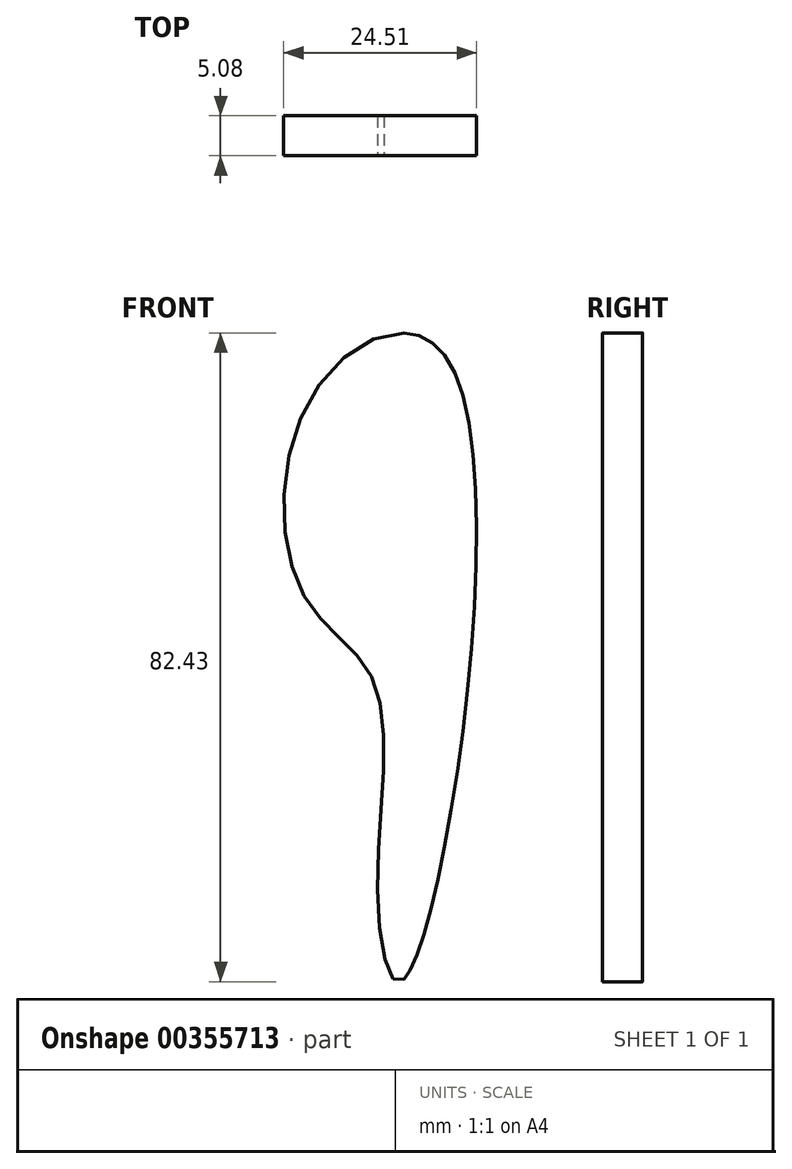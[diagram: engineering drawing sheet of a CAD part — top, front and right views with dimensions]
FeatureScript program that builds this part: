
annotation { "Feature Type Name" : "Feature", "Feature Type Description" : "" }
export const myFeature = defineFeature(function(context is Context, id is Id, definition is map)
    precondition{}
    {
        {
            var Q0;
            Q0=qCreatedBy(makeId("Front.planeOp"),FACE);
            var sketch = newSketch(context, id + "F0", { "sketchPlane" : qUnion([Q0])});
            skFitSpline(sketch, "E0", {"points": [v(0, 0) * mm, v(-3.3, 9.88) * mm, v(-3.77, 37.65) * mm, v(-12.94, 49.18) * mm, v(-10.59, 75.77) * mm, v(5.65, 78.6) * mm, v(0, 0) * mm]});
            skLineSegment(sketch, "E1", {"start": v(0, 0) * mm, "end": v(0, 82.1) * mm});
            skSolve(sketch);
        }
        {
            var Q0;
            Q0=makeQuery(id+"F0.imprint","IMPRINT",FACE,{"disambiguationData":[TD([[makeQuery(id+"F0.imprint","IMPRINT",EDGE,{"derivedFrom":sQuery(id+"F0.wireOp",EDGE,"E0")}),-1.0]])]});
            extrude(context, id + "F1", {"entities" : qUnion([Q0]), "depth" : 5.08 * mm});
        }
    });
